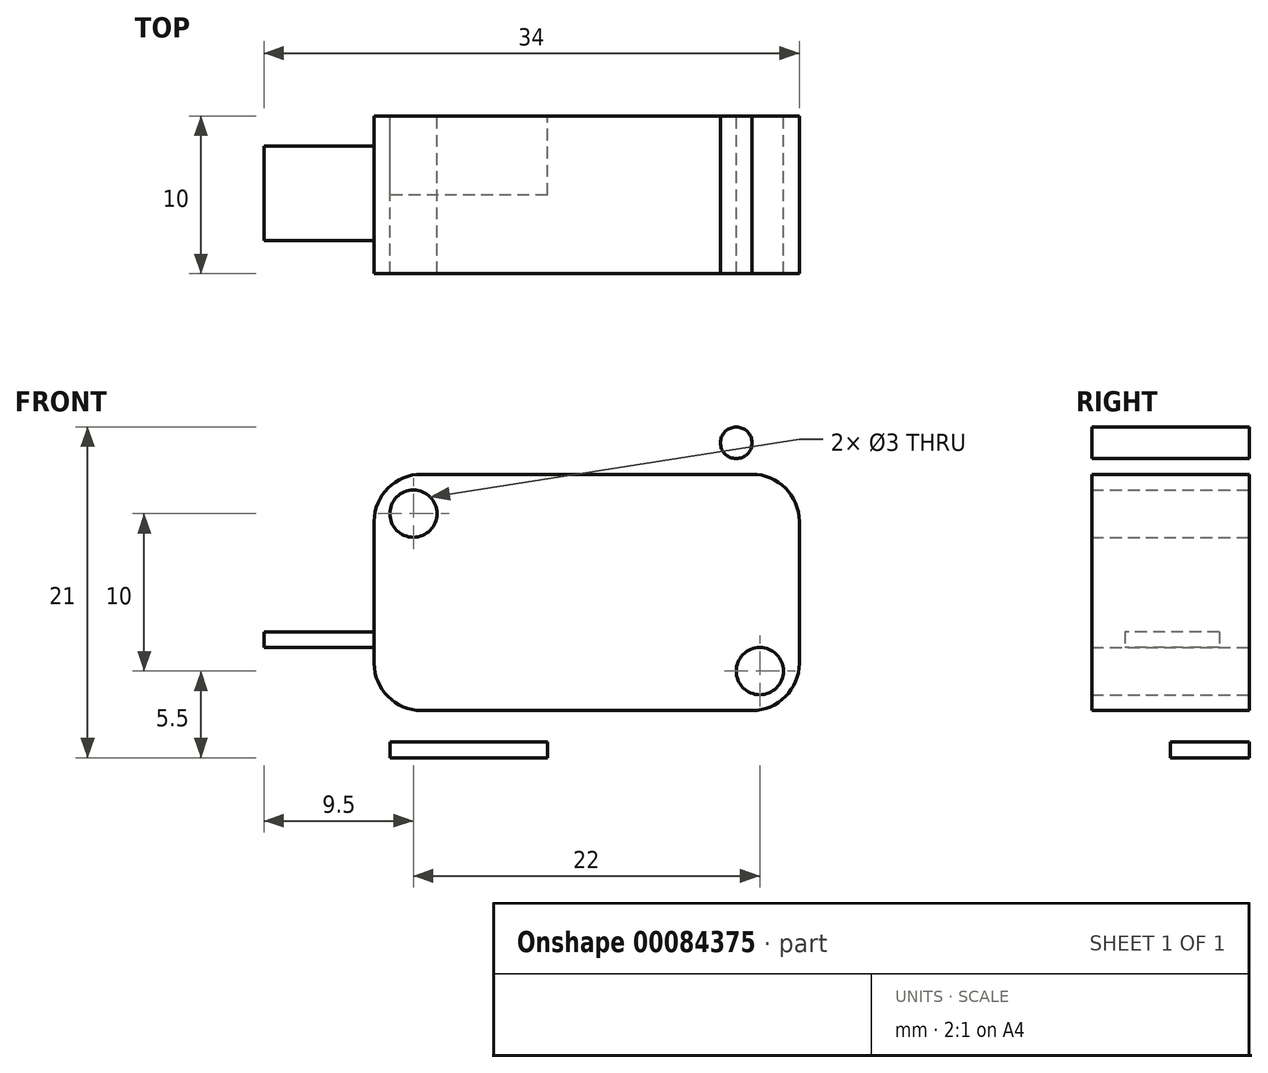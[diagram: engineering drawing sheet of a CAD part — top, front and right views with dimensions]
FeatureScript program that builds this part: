
annotation { "Feature Type Name" : "Feature", "Feature Type Description" : "" }
export const myFeature = defineFeature(function(context is Context, id is Id, definition is map)
    precondition{}
    {
        {
            var Q0;
            Q0=qCreatedBy(makeId("Front.planeOp"),FACE);
            var sketch = newSketch(context, id + "F0", { "sketchPlane" : qUnion([Q0])});
            skLineSegment(sketch, "E0.bottom", {"start": v(-10.5, 7.5) * mm, "end": v(10.5, 7.5) * mm});
            skLineSegment(sketch, "E0.top", {"start": v(-10.5, -7.5) * mm, "end": v(10.5, -7.5) * mm});
            skLineSegment(sketch, "E0.left", {"start": v(-13.5, 4.5) * mm, "end": v(-13.5, -4.5) * mm});
            skLineSegment(sketch, "E0.right", {"start": v(13.5, 4.5) * mm, "end": v(13.5, -4.5) * mm});
            skPoint(sketch, "E0.middle", {"position": v(0, 0) * mm});
            skLineSegment(sketch, "E1.bottom", {"start": v(-2.5, -7.5) * mm, "end": v(-1.5, -7.5) * mm});
            skLineSegment(sketch, "E1.top", {"start": v(-2.5, -10.5) * mm, "end": v(-1.5, -10.5) * mm});
            skLineSegment(sketch, "E1.left", {"start": v(-2.5, -7.5) * mm, "end": v(-2.5, -10.5) * mm});
            skLineSegment(sketch, "E1.right", {"start": v(-1.5, -7.5) * mm, "end": v(-1.5, -10.5) * mm});
            skLineSegment(sketch, "E2.bottom", {"start": v(-2.5, -10.5) * mm, "end": v(-12.5, -10.5) * mm});
            skLineSegment(sketch, "E2.top", {"start": v(-2.5, -9.5) * mm, "end": v(-12.5, -9.5) * mm});
            skLineSegment(sketch, "E2.left", {"start": v(-2.5, -10.5) * mm, "end": v(-2.5, -9.5) * mm});
            skLineSegment(sketch, "E2.right", {"start": v(-12.5, -10.5) * mm, "end": v(-12.5, -9.5) * mm});
            skLineSegment(sketch, "E3.bottom", {"start": v(2.5, 7.5) * mm, "end": v(3.5, 7.5) * mm});
            skLineSegment(sketch, "E3.top", {"start": v(2.5, 9.5) * mm, "end": v(3.5, 9.5) * mm});
            skLineSegment(sketch, "E3.left", {"start": v(2.5, 7.5) * mm, "end": v(2.5, 9.5) * mm});
            skLineSegment(sketch, "E3.right", {"start": v(3.5, 7.5) * mm, "end": v(3.5, 9.5) * mm});
            skLineSegment(sketch, "E4", {"start": v(174.54, 101.68) * mm, "end": v(176.09, 98.8) * mm});
            skCircle(sketch, "E5", {"center": v(-11, 5) * mm, "radius": 1.5 * mm});
            skCircle(sketch, "E6", {"center": v(11, -5) * mm, "radius": 1.5 * mm});
            skLineSegment(sketch, "E7.bottom", {"start": v(10.5, 7.5) * mm, "end": v(8.5, 7.5) * mm});
            skLineSegment(sketch, "E7.top", {"start": v(10.5, 9.5) * mm, "end": v(8.5, 9.5) * mm});
            skLineSegment(sketch, "E7.left", {"start": v(10.5, 7.5) * mm, "end": v(10.5, 9.5) * mm});
            skLineSegment(sketch, "E7.right", {"start": v(8.5, 7.5) * mm, "end": v(8.5, 9.5) * mm});
            skCircle(sketch, "E8", {"center": v(9.5, 9.5) * mm, "radius": 1 * mm});
            skLineSegment(sketch, "E9.bottom", {"start": v(-13.5, -2.5) * mm, "end": v(-24.5, -2.5) * mm});
            skLineSegment(sketch, "E9.top", {"start": v(-13.5, -3.5) * mm, "end": v(-24.5, -3.5) * mm});
            skLineSegment(sketch, "E9.left", {"start": v(-13.5, -2.5) * mm, "end": v(-13.5, -3.5) * mm});
            skLineSegment(sketch, "E9.right", {"start": v(-24.5, -2.5) * mm, "end": v(-24.5, -3.5) * mm});
            skLineSegment(sketch, "E10", {"start": v(3.5, 9.5) * mm, "end": v(53.8, 18) * mm});
            skLineSegment(sketch, "E11", {"start": v(2.5, 9.5) * mm, "end": v(53.8, 18.17) * mm});
            skPoint(sketch, "E12.visualSharp", {"position": v(-13.5, 7.5) * mm});
            skArc(sketch, "E12.filletArc", {"start": v(-10.5, 7.5) * mm, "mid": v(-12.62, 6.62) * mm, "end": v(-13.5, 4.5) * mm});
            skPoint(sketch, "E13.visualSharp", {"position": v(13.5, -7.5) * mm});
            skArc(sketch, "E13.filletArc", {"start": v(10.5, -7.5) * mm, "mid": v(12.62, -6.62) * mm, "end": v(13.5, -4.5) * mm});
            skPoint(sketch, "E14.visualSharp", {"position": v(-13.5, -7.5) * mm});
            skArc(sketch, "E14.filletArc", {"start": v(-13.5, -4.5) * mm, "mid": v(-12.62, -6.62) * mm, "end": v(-10.5, -7.5) * mm});
            skPoint(sketch, "E15.visualSharp", {"position": v(13.5, 7.5) * mm});
            skArc(sketch, "E15.filletArc", {"start": v(13.5, 4.5) * mm, "mid": v(12.62, 6.62) * mm, "end": v(10.5, 7.5) * mm});
            skSolve(sketch);
        }
        {
            var Q0;
            Q0=makeQuery(id+"F0.imprint","IMPRINT",FACE,{"disambiguationData":[TD([[makeQuery(id+"F0.imprint","IMPRINT",EDGE,{"derivedFrom":sQuery(id+"F0.wireOp",EDGE,"E0.right")}),-1.0]])]});
            extrude(context, id + "F1", {"entities" : qUnion([Q0]), "depth" : 10 * mm});
        }
        {
            var Q0;
            Q0=makeQuery(id+"F0.imprint","IMPRINT",FACE,{"disambiguationData":[TD([[makeQuery(id+"F0.imprint","IMPRINT",EDGE,{"derivedFrom":sQuery(id+"F0.wireOp",EDGE,"E2.bottom")}),-1.0]])]});
            var Q1;
            Q1=makeQuery(id+"F0.imprint","IMPRINT",FACE,{"disambiguationData":[TD([[makeQuery(id+"F0.imprint","IMPRINT",EDGE,{"derivedFrom":sQuery(id+"F0.wireOp",EDGE,"E1.bottom")}),-1.0]])]});
            extrude(context, id + "F2", {"entities" : qUnion([Q0, Q1]), "depth" : 5 * mm});
        }
        {
            var Q0;
            Q0=makeQuery(id+"F1.opExtrude","SWEPT_FACE",FACE,{"disambiguationData":[OSD([sQuery(id+"F0.wireOp",EDGE,"E0.left"),sQuery(id+"F0.wireOp",EDGE,"E9.left")])]});
            var sketch = newSketch(context, id + "F3", { "sketchPlane" : qUnion([Q0])});
            skLineSegment(sketch, "E16.bottom", {"start": v(1.9, -2.5) * mm, "end": v(7.9, -2.5) * mm});
            skLineSegment(sketch, "E16.top", {"start": v(1.9, -3.5) * mm, "end": v(7.9, -3.5) * mm});
            skLineSegment(sketch, "E16.left", {"start": v(1.9, -2.5) * mm, "end": v(1.9, -3.5) * mm});
            skLineSegment(sketch, "E16.right", {"start": v(7.9, -2.5) * mm, "end": v(7.9, -3.5) * mm});
            skSolve(sketch);
        }
        {
            var Q0;
            Q0=makeQuery(id+"F3.imprint","IMPRINT",FACE,{"disambiguationData":[TD([[makeQuery(id+"F3.imprint","IMPRINT",EDGE,{"derivedFrom":sQuery(id+"F3.wireOp",EDGE,"E16.bottom")}),-1.0]])]});
            extrude(context, id + "F4", {"entities" : qUnion([Q0]), "operationType" : NewBodyOperationType.ADD, "depth" : 7 * mm});
        }
        {
            var Q0;
            Q0=makeQuery(id+"F0.imprint","IMPRINT",FACE,{"disambiguationData":[TD([[makeQuery(id+"F0.imprint","IMPRINT",EDGE,{"derivedFrom":sQuery(id+"F0.wireOp",EDGE,"E7.bottom")}),-1.0]])]});
            var Q1;
            {var subQ0=sQuery(id+"F0.wireOp",EDGE,"E7.top");Q1=makeQuery(id+"F0.imprint","IMPRINT",FACE,{"disambiguationData":[TD([[makeQuery(id+"F0.imprint","IMPRINT",EDGE,{"derivedFrom":subQ0}),1.0]])]});}
            var Q2;
            {var subQ0=sQuery(id+"F0.wireOp",EDGE,"E7.top");Q2=makeQuery(id+"F0.imprint","IMPRINT",FACE,{"disambiguationData":[TD([[makeQuery(id+"F0.imprint","IMPRINT",EDGE,{"derivedFrom":subQ0}),-1.0]])]});}
            extrude(context, id + "F5", {"entities" : qUnion([Q0, Q1, Q2]), "operationType" : NewBodyOperationType.ADD, "depth" : 10 * mm});
        }
    });
